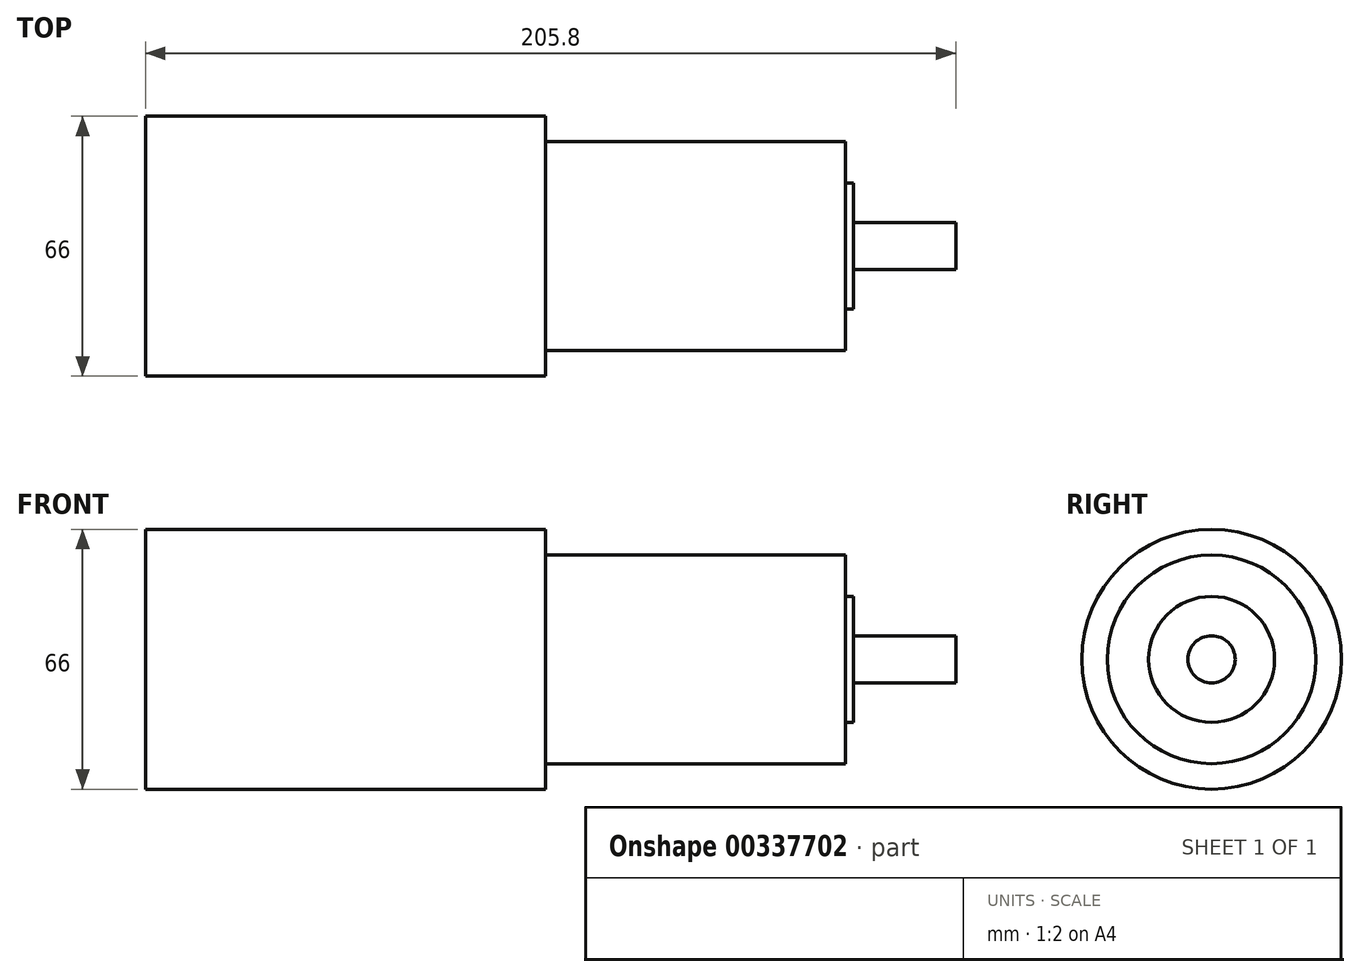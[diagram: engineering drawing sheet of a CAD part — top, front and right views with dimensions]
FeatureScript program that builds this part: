
annotation { "Feature Type Name" : "Feature", "Feature Type Description" : "" }
export const myFeature = defineFeature(function(context is Context, id is Id, definition is map)
    precondition{}
    {
        {
            var Q0;
            Q0=qCreatedBy(makeId("Right.planeOp"),FACE);
            var sketch = newSketch(context, id + "F0", { "sketchPlane" : qUnion([Q0])});
            skCircle(sketch, "E0", {"center": v(0, 0) * mm, "radius": 33 * mm});
            skSolve(sketch);
        }
        {
            var Q0;
            Q0=qSketchRegion(id+"F0",true);
            extrude(context, id + "F1", {"entities" : qUnion([Q0]), "depth" : 101.6 * mm});
        }
        {
            var Q0;
            Q0=makeQuery(id+"F1.opExtrude","CAP_FACE",FACE,{"disambiguationData":[OSD([sQuery(id+"F0.wireOp",EDGE,"E0")])],"isStart":false});
            var sketch = newSketch(context, id + "F2", { "sketchPlane" : qUnion([Q0])});
            skCircle(sketch, "E1", {"center": v(0, 0) * mm, "radius": 26.5 * mm});
            skSolve(sketch);
        }
        {
            var Q0;
            Q0=qSketchRegion(id+"F2",true);
            extrude(context, id + "F3", {"entities" : qUnion([Q0]), "operationType" : NewBodyOperationType.ADD, "depth" : 76.2 * mm});
        }
        {
            var Q0;
            Q0=makeQuery(id+"F3.opExtrude","CAP_FACE",FACE,{"disambiguationData":[OSD([sQuery(id+"F2.wireOp",EDGE,"E1")])],"isStart":false});
            var sketch = newSketch(context, id + "F4", { "sketchPlane" : qUnion([Q0])});
            skCircle(sketch, "E2", {"center": v(0, 0) * mm, "radius": 16 * mm});
            skSolve(sketch);
        }
        {
            var Q0;
            Q0=qSketchRegion(id+"F4",true);
            extrude(context, id + "F5", {"entities" : qUnion([Q0]), "operationType" : NewBodyOperationType.ADD, "depth" : 2 * mm});
        }
        {
            var Q0;
            Q0=makeQuery(id+"F5.opExtrude","CAP_FACE",FACE,{"disambiguationData":[OSD([sQuery(id+"F4.wireOp",EDGE,"E2")])],"isStart":false});
            var sketch = newSketch(context, id + "F6", { "sketchPlane" : qUnion([Q0])});
            skCircle(sketch, "E3", {"center": v(0, 0) * mm, "radius": 6 * mm});
            skSolve(sketch);
        }
        {
            var Q0;
            Q0=qSketchRegion(id+"F6",true);
            extrude(context, id + "F7", {"entities" : qUnion([Q0]), "operationType" : NewBodyOperationType.ADD, "depth" : 26 * mm});
        }
    });
